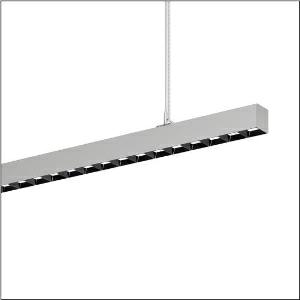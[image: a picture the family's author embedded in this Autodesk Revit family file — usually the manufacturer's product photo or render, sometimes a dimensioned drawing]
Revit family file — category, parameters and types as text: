
# Revit family: silica_r__21_51mx32tat7s_c957
name_source: partatom
category: Lighting Fixtures
units: mm (PartAtom-declared; Revit-internal decimal feet)

## family parameters
Cut with Voids When Loaded = No
Host = Face
Light Source = No
Part Type = Normal
Room Calculation Point = No
Round Connector Dimension = Use Diameter
Shared = No

## types (1)
- --- (1 x LED, 6220 lm, 53.4 W, 6500K)
    Apparent Load = 53 VA
    CIE Flux Codes = 84 99 100 60 100
    Color Rendering = 80
    Color Temperature = 6500K
    Default Elevation = 1800 mm
    Description = Silica® 21, office luminaire, primary light control with darklight reflector, of PMMA, black, CAT 2 (L<= 3000cd/m²), light emission: direct/indirect distribution, primary light characteristic: symmetric, installation type: suspended mounting, LED, rated luminous flux: 6.220lm, luminous efficacy: 111lm/W, light colour: 8tw, colour temperature: 2700..6500K, control gear: ECG DALI, with terminal, 3+2-pole, max. 2.5mm², mains connection: 220..240V, AC, 50/60Hz, rated input power: 56.1W, luminaire housing, of aluminium, metallic grey (RAL 9006), length: 1.204mm, width: 53mm, height: 53mm, protection rating (complete): IP20, insulation class (complete): insulation class I (protective earthing), certification: CE, permissible operating ambient temperature: 0..+35°C, standard: EN 50419, packaging unit: 1 piece
    Height = 53 mm
    Lamp = 1 x LED
    Lamp Light Flux = 6220 lm
    Lamp Power = 53.4 W
    Lamp count = 1
    Length = 1204 mm
    Luminous efficacy = 116 lm/W
    Manufacturer = Siteco
    ModVariant = No
    Model = 51MX32TAT7S
    Mounting Place = Ceiling
    Mounting Type = Pendant
    Number of Poles = 1
    OnlyDefault = Yes
    Power Factor = 1
    Product Name = Silica® 21
    Product group = office luminaire | ceiling pendant
    ProductGroupID = 902
    Protection Class = Protection class I
    Protection Degree = IP 20
    RLX_Detail_Level = 1
    RLX_Emergency_Light_Flux = 0 lm
    RLX_Emergency_Type = 0
    RLX_Emergency_Type_DB = No
    RlxData = <blob elided: 41125 chars, md5=48849548>
    Socket = socket
    Standby Power = 0 W
    System Light Flux = 6220 lm
    System Power = 53 W
    Type Comments = individual setting
    Type Image = l_1313642.jpg
    URL = http://relux.com
    VarID = @adj_089295
    Voltage = 0 V
    Weight = 0.00 kg
    Width = 53 mm

## geometry (parser evidence)
native form markers: Blend x4, Sweep x12
no freeform markers — native parametric forms only
